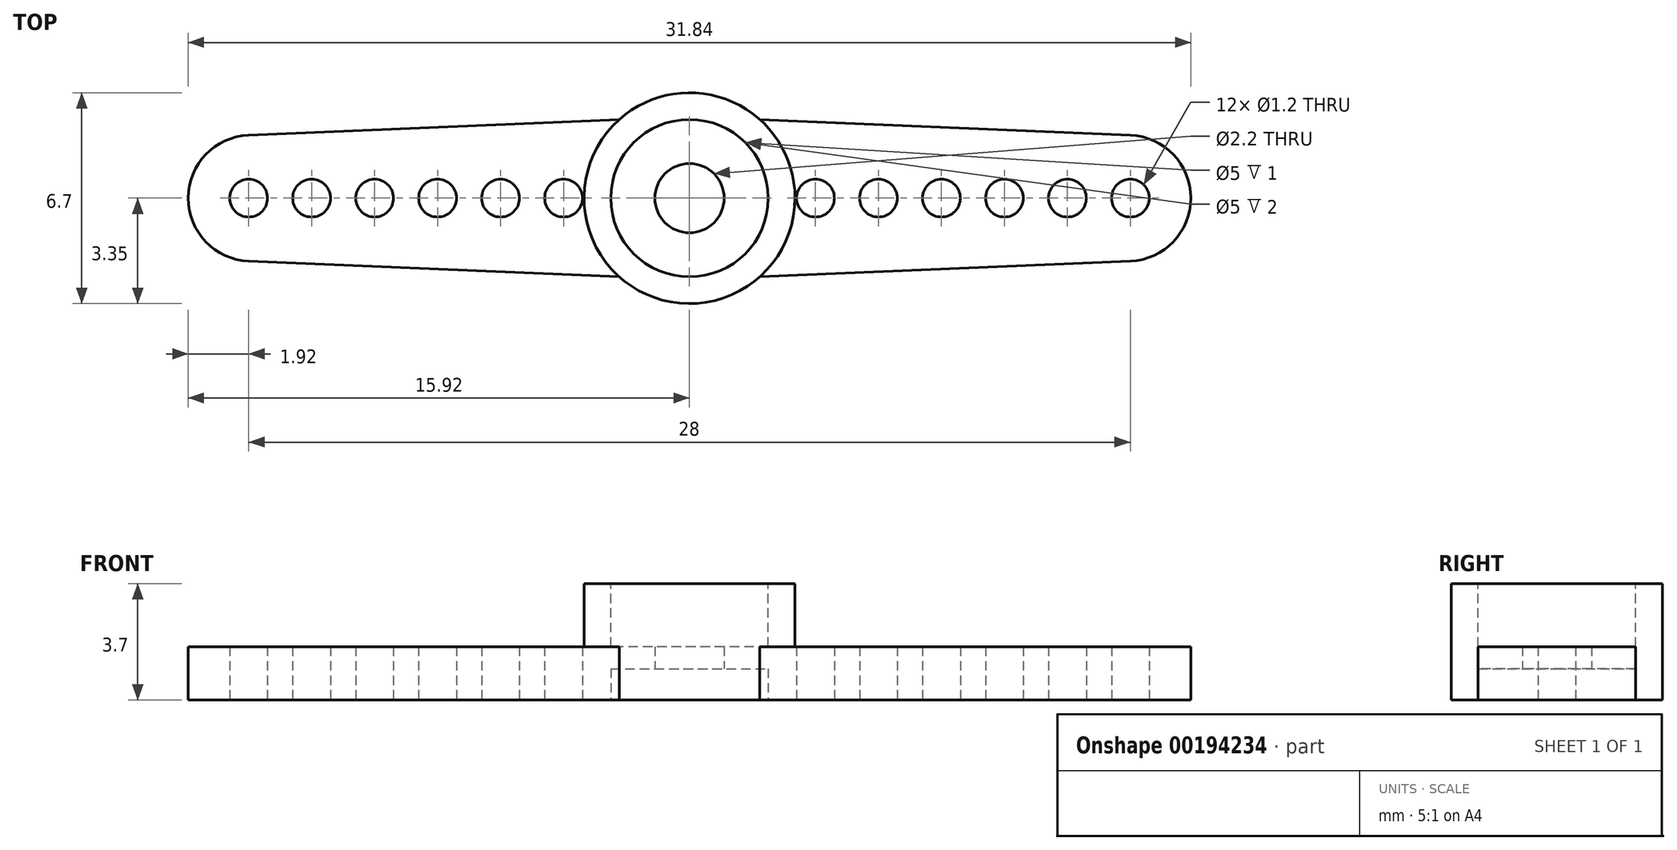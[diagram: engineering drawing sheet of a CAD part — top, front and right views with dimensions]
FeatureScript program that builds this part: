
annotation { "Feature Type Name" : "Feature", "Feature Type Description" : "" }
export const myFeature = defineFeature(function(context is Context, id is Id, definition is map)
    precondition{}
    {
        {
            var Q0;
            Q0=qCreatedBy(makeId("Top.planeOp"),FACE);
            var sketch = newSketch(context, id + "F0", { "sketchPlane" : qUnion([Q0])});
            skCircle(sketch, "E0", {"center": v(0, 0) * mm, "radius": 3.35 * mm});
            skLineSegment(sketch, "E1", {"start": v(0, 0) * mm, "end": v(-2.56, 0) * mm, "construction": true});
            skLineSegment(sketch, "E2", {"start": v(0, 0) * mm, "end": v(6, 0) * mm, "construction": true});
            skCircle(sketch, "E3", {"center": v(6, 0) * mm, "radius": 0.6 * mm});
            skCircle(sketch, "E4.1.0.0", {"center": v(8, 0) * mm, "radius": 0.6 * mm});
            skCircle(sketch, "E4.2.0.0", {"center": v(10, 0) * mm, "radius": 0.6 * mm});
            skCircle(sketch, "E4.3.0.0", {"center": v(12, 0) * mm, "radius": 0.6 * mm});
            skCircle(sketch, "E4.4.0.0", {"center": v(14, 0) * mm, "radius": 0.6 * mm});
            skLineSegment(sketch, "E4.direction1", {"start": v(6, 0) * mm, "end": v(8, 0) * mm, "construction": true});
            skCircle(sketch, "E5.1.0.0", {"center": v(4, 0) * mm, "radius": 0.6 * mm});
            skLineSegment(sketch, "E5.direction1", {"start": v(6, 0) * mm, "end": v(4, 0) * mm, "construction": true});
            skLineSegment(sketch, "E6", {"start": v(14, 2) * mm, "end": v(2.23, 2.5) * mm});
            skLineSegment(sketch, "E7.MirrorCS", {"start": v(14, -2) * mm, "end": v(2.23, -2.5) * mm});
            skArc(sketch, "E8", {"start": v(14, 2) * mm, "mid": v(15.92, 0) * mm, "end": v(14, -2) * mm});
            skLineSegment(sketch, "E9", {"start": v(0, 5) * mm, "end": v(0, -4.95) * mm, "construction": true});
            skLineSegment(sketch, "E10.MirrorCS", {"start": v(-14, 2) * mm, "end": v(-2.23, 2.5) * mm});
            skCircle(sketch, "E11.MirrorC", {"center": v(-4, 0) * mm, "radius": 0.6 * mm});
            skLineSegment(sketch, "E12.MirrorCS", {"start": v(-14, -2) * mm, "end": v(-2.23, -2.5) * mm});
            skCircle(sketch, "E13.MirrorC", {"center": v(-6, 0) * mm, "radius": 0.6 * mm});
            skCircle(sketch, "E14.MirrorC", {"center": v(-8, 0) * mm, "radius": 0.6 * mm});
            skCircle(sketch, "E15.MirrorC", {"center": v(-10, 0) * mm, "radius": 0.6 * mm});
            skCircle(sketch, "E16.MirrorC", {"center": v(-12, 0) * mm, "radius": 0.6 * mm});
            skCircle(sketch, "E17.MirrorC", {"center": v(-14, 0) * mm, "radius": 0.6 * mm});
            skArc(sketch, "E18.MirrorCS", {"start": v(-14, 2) * mm, "mid": v(-15.92, 0) * mm, "end": v(-14, -2) * mm});
            skSolve(sketch);
        }
        {
            var Q0;
            Q0=qSketchRegion(id+"F0",true);
            extrude(context, id + "F1", {"entities" : qUnion([Q0]), "depth" : 1.7 * mm});
        }
        {
            var Q0;
            Q0=makeQuery(id+"F1.opExtrude","CAP_FACE",FACE,{"disambiguationData":[OSD([sQuery(id+"F0.wireOp",EDGE,"E0"),sQuery(id+"F0.wireOp",EDGE,"E3"),sQuery(id+"F0.wireOp",EDGE,"E4.1.0.0"),sQuery(id+"F0.wireOp",EDGE,"E4.2.0.0"),sQuery(id+"F0.wireOp",EDGE,"E4.3.0.0"),sQuery(id+"F0.wireOp",EDGE,"E4.4.0.0"),sQuery(id+"F0.wireOp",EDGE,"E5.1.0.0"),sQuery(id+"F0.wireOp",EDGE,"E6"),sQuery(id+"F0.wireOp",EDGE,"E7.MirrorCS"),sQuery(id+"F0.wireOp",EDGE,"E8")])],"isStart":false});
            var sketch = newSketch(context, id + "F2", { "sketchPlane" : qUnion([Q0])});
            skCircle(sketch, "E19", {"center": v(0, 0) * mm, "radius": 3.35 * mm});
            skPoint(sketch, "E19.first.point", {"position": v(2.23, 2.5) * mm});
            skPoint(sketch, "E19.second.point", {"position": v(2.23, -2.5) * mm});
            skPoint(sketch, "E19.third.point", {"position": v(-3.35, 0.14) * mm});
            skSolve(sketch);
        }
        {
            var Q0;
            Q0=qSketchRegion(id+"F2",true);
            extrude(context, id + "F3", {"entities" : qUnion([Q0]), "operationType" : NewBodyOperationType.ADD, "depth" : 2 * mm});
        }
        {
            var Q0;
            Q0=makeQuery(id+"F1.opExtrude","CAP_FACE",FACE,{"disambiguationData":[OSD([sQuery(id+"F0.wireOp",EDGE,"E0"),sQuery(id+"F0.wireOp",EDGE,"E3"),sQuery(id+"F0.wireOp",EDGE,"E4.1.0.0"),sQuery(id+"F0.wireOp",EDGE,"E4.2.0.0"),sQuery(id+"F0.wireOp",EDGE,"E4.3.0.0"),sQuery(id+"F0.wireOp",EDGE,"E4.4.0.0"),sQuery(id+"F0.wireOp",EDGE,"E5.1.0.0"),sQuery(id+"F0.wireOp",EDGE,"E6"),sQuery(id+"F0.wireOp",EDGE,"E7.MirrorCS"),sQuery(id+"F0.wireOp",EDGE,"E8")])],"isStart":true});
            var sketch = newSketch(context, id + "F4", { "sketchPlane" : qUnion([Q0])});
            skCircle(sketch, "E20", {"center": v(0, 0) * mm, "radius": 2.5 * mm});
            skSolve(sketch);
        }
        {
            var Q0;
            Q0=qSketchRegion(id+"F4",true);
            extrude(context, id + "F5", {"entities" : qUnion([Q0]), "operationType" : NewBodyOperationType.REMOVE, "oppositeDirection" : true, "depth" : 1 * mm});
        }
        {
            var Q0;
            Q0=makeQuery(id+"F5.boolean.opBoolean","COPY",FACE,{"derivedFrom":makeQuery(id+"F5.opExtrude","CAP_FACE",FACE,{"disambiguationData":[OSD([sQuery(id+"F4.wireOp",EDGE,"E20")])],"isStart":false})});
            var sketch = newSketch(context, id + "F6", { "sketchPlane" : qUnion([Q0])});
            skCircle(sketch, "E21", {"center": v(0, 0) * mm, "radius": 1.1 * mm});
            skSolve(sketch);
        }
        {
            var Q0;
            Q0=qSketchRegion(id+"F6",true);
            extrude(context, id + "F7", {"entities" : qUnion([Q0]), "operationType" : NewBodyOperationType.REMOVE, "endBound" : BoundingType.THROUGH_ALL, "oppositeDirection" : true, "depth" : 1 * mm});
        }
        {
            var Q0;
            Q0=makeQuery(id+"F3.opExtrude","CAP_FACE",FACE,{"disambiguationData":[OSD([sQuery(id+"F2.wireOp",EDGE,"E19")])],"isStart":false});
            var sketch = newSketch(context, id + "F8", { "sketchPlane" : qUnion([Q0])});
            skCircle(sketch, "E22", {"center": v(0, 0) * mm, "radius": 2.5 * mm});
            skSolve(sketch);
        }
        {
            var Q0;
            Q0=qSketchRegion(id+"F8",true);
            extrude(context, id + "F9", {"entities" : qUnion([Q0]), "operationType" : NewBodyOperationType.REMOVE, "oppositeDirection" : true, "depth" : 2 * mm});
        }
    });
